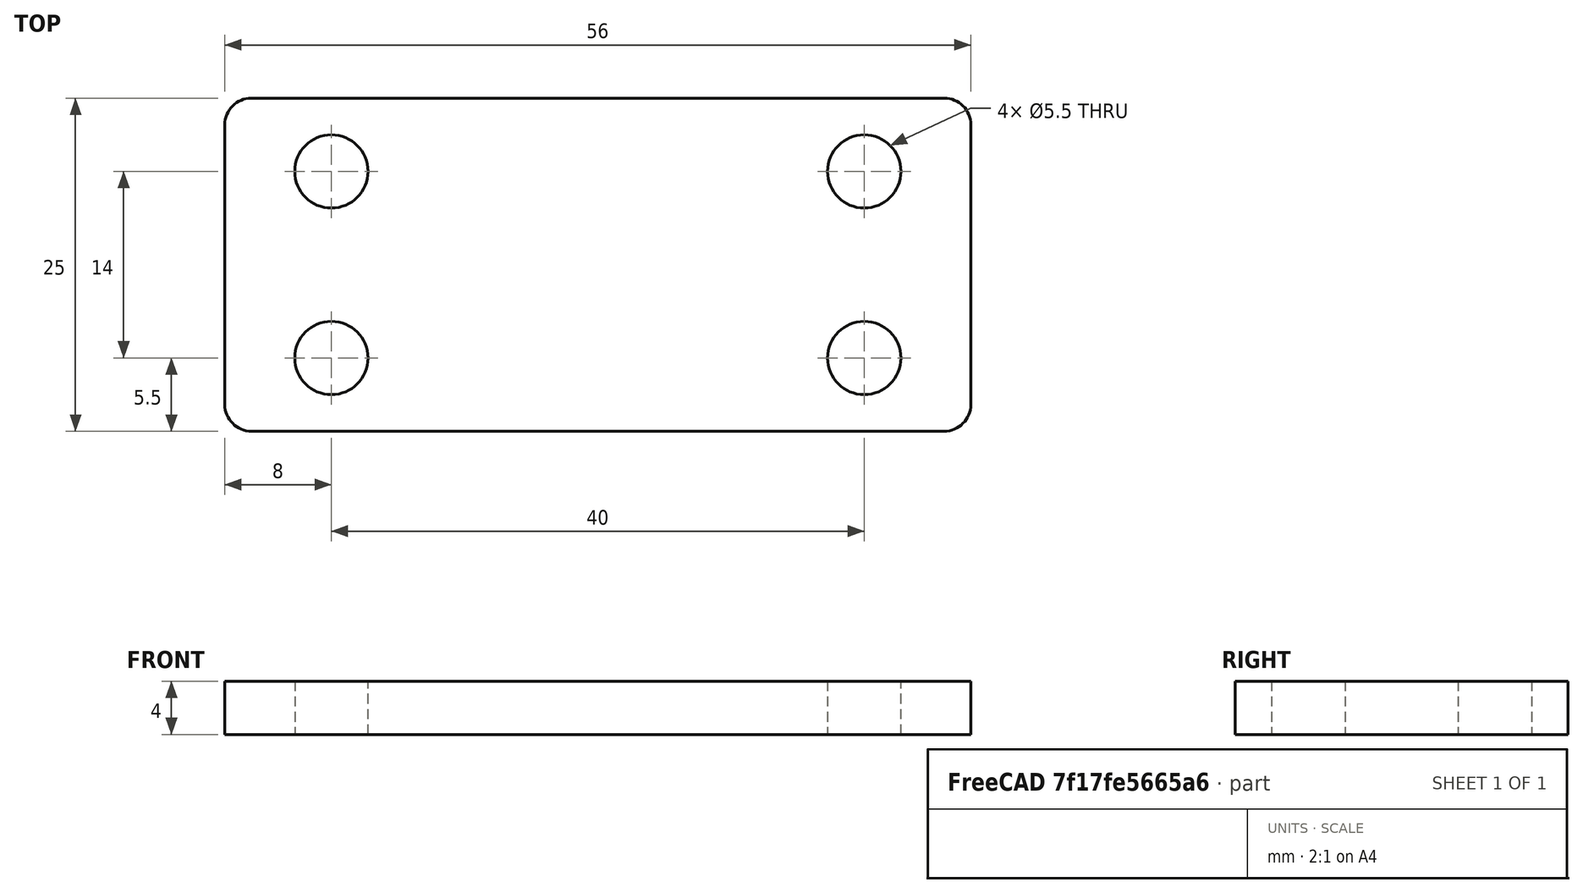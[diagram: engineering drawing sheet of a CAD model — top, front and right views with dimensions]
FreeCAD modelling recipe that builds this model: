
FCSTD DOCUMENT  (FreeCAD 0.19R24267 +99 (Git))
Label: V2 Clamp elastic retaining plate 4 holes
License: All rights reserved
LicenseURL: http://en.wikipedia.org/wiki/All_rights_reserved
objects: Sketcher::SketchObject×1, PartDesign::Pad×1, PartDesign::Body×1
note: 4 computed .brp shape members not serialized (recipe doc carries the construction recipe); baked Part::Feature solids carry a one-line shape summary decoded from their .brp

FEATURE [Sketcher::SketchObject] Sketch
  FullyConstrained = true
  MapMode = 5
  Support = -> [XY_Plane]
  sketch-geometry (17):
    g0: LineSegment StartX=-6 StartY=12.5 StartZ=0 EndX=46 EndY=12.5 EndZ=0
    g1: LineSegment StartX=48 StartY=10.5 StartZ=0 EndX=48 EndY=-10.5 EndZ=0
    g2: LineSegment StartX=46 StartY=-12.5 StartZ=0 EndX=-6 EndY=-12.5 EndZ=0
    g3: LineSegment StartX=-8 StartY=-10.5 StartZ=0 EndX=-8 EndY=10.5 EndZ=0
    g4: ArcOfCircle CenterX=-6 CenterY=10.5 CenterZ=0 NormalX=0 NormalY=0 NormalZ=1 AngleXU=0 Radius=2 StartAngle=1.5708 EndAngle=3.14159
    g5: ArcOfCircle CenterX=-6 CenterY=-10.5 CenterZ=0 NormalX=0 NormalY=0 NormalZ=1 AngleXU=0 Radius=2 StartAngle=3.14159 EndAngle=4.71239
    g6: ArcOfCircle CenterX=46 CenterY=-10.5 CenterZ=0 NormalX=0 NormalY=0 NormalZ=1 AngleXU=0 Radius=2 StartAngle=4.71239 EndAngle=6.28319
    g7: ArcOfCircle CenterX=46 CenterY=10.5 CenterZ=0 NormalX=0 NormalY=0 NormalZ=1 AngleXU=0 Radius=2 StartAngle=0 EndAngle=1.5708
    g8: LineSegment StartX=0 StartY=0 StartZ=0 EndX=-8 EndY=0 EndZ=0
    g9: LineSegment StartX=40 StartY=0 StartZ=0 EndX=48 EndY=0 EndZ=0
    g10: Circle CenterX=0 CenterY=7 CenterZ=0 NormalX=0 NormalY=0 NormalZ=1 AngleXU=0 Radius=2.75
    g11: Circle CenterX=0 CenterY=-7 CenterZ=0 NormalX=0 NormalY=0 NormalZ=1 AngleXU=0 Radius=2.75
    g12: LineSegment StartX=40 StartY=7 StartZ=0 EndX=40 EndY=-7 EndZ=0
    g13: LineSegment StartX=0 StartY=7 StartZ=0 EndX=40 EndY=7 EndZ=0
    g14: LineSegment StartX=40 StartY=-7 StartZ=0 EndX=0 EndY=-7 EndZ=0
    g15: Circle CenterX=40 CenterY=7 CenterZ=0 NormalX=0 NormalY=0 NormalZ=1 AngleXU=0 Radius=2.75
    g16: Circle CenterX=40 CenterY=-7 CenterZ=0 NormalX=0 NormalY=0 NormalZ=1 AngleXU=0 Radius=2.75
  constraints (43):
    c: Horizontal(g0)
    c: Horizontal(g2)
    c: Vertical(g1)
    c: Tangent(g3,g4) = 1.5708
    c: Tangent(g0,g4) = 1.5708
    c: Tangent(g3,g5) = 1.5708
    c: Tangent(g2,g5) = 1.5708
    c: Tangent(g1,g6) = 1.5708
    c: Tangent(g2,g6) = 1.5708
    c: Tangent(g0,g7) = 1.5708
    c: Tangent(g1,g7) = 1.5708
    c: DistanceY(g2,g0) = 25
    c: Symmetric(g0,g2,g-1)
    c: Vertical(g3)
    c: Equal(g4,g7)
    c: Equal(g7,g6)
    c: Radius(g4) = 2
    c: PointOnObject(g8,g3)
    c: Horizontal(g8)
    c: PointOnObject(g9,g1)
    c: Horizontal(g9)
    c: Equal(g9,g8)
    c: DistanceX(g9,g9) = 8
    c: PointOnObject(g10,g-2)
    c: PointOnObject(g11,g-2)
    c: Symmetric(g12,g12,g-1)
    c: DistanceY(g12,g12) = 14
    c: Coincident(g13,g10)
    c: Coincident(g13,g12)
    c: Coincident(g14,g12)
    c: Coincident(g14,g11)
    c: Horizontal(g14)
    c: Horizontal(g13)
    c: DistanceX(g14,g14) = 40
    c: Coincident(g15,g12)
    c: Coincident(g16,g12)
    c: Equal(g10,g11)
    c: Equal(g11,g15)
    c: Equal(g15,g16)
    c: Coincident(g8,g-1)
    c: PointOnObject(g9,g12)
    c: PointOnObject(g9,g-1)
    c: Diameter(g15) = 5.5
FEATURE [PartDesign::Pad] Pad
  Direction = (1,1,1)
  Length = 4
  Length2 = 100
  Profile = -> Sketch
  Type = 0
FEATURE [PartDesign::Body] Body
  Group = -> [Sketch,Pad]
  Origin = -> Origin
  Tip = -> Pad
